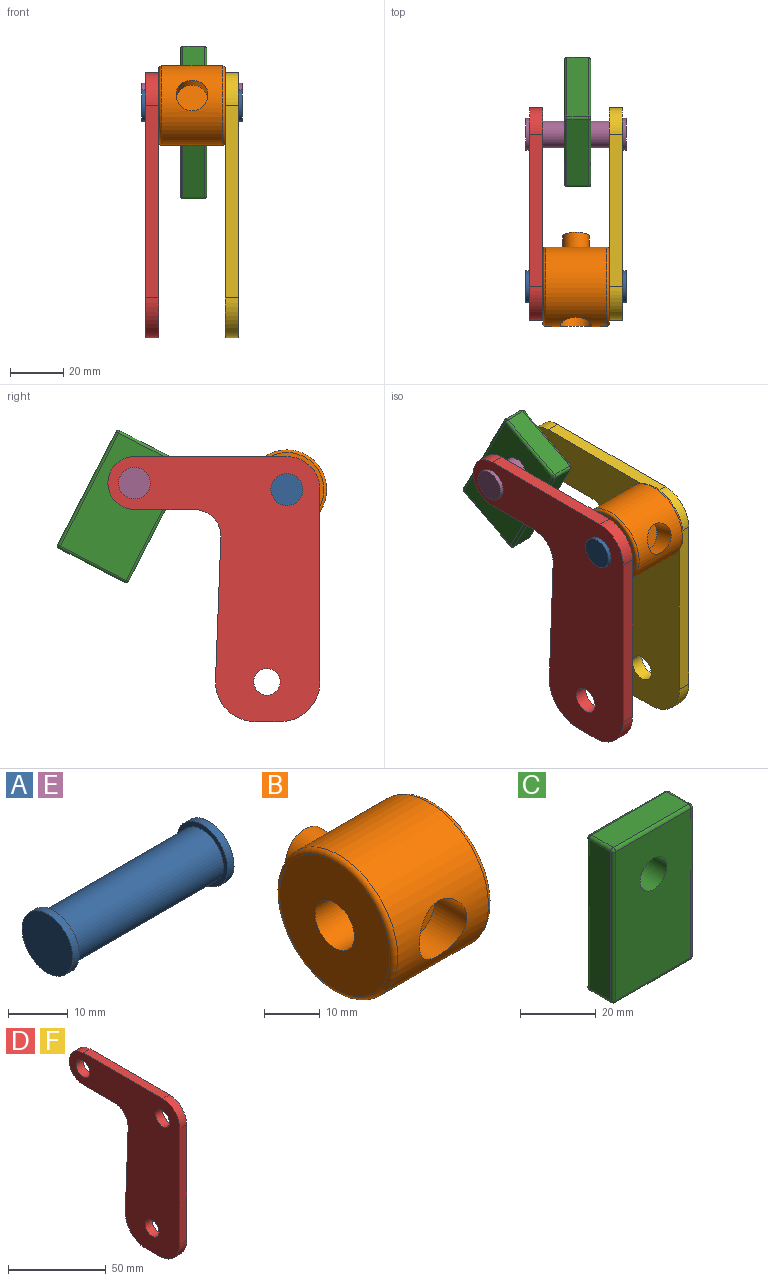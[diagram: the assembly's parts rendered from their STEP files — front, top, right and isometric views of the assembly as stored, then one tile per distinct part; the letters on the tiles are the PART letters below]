
ASSEMBLY  parts=6 mates=6
PART A: 7 faces, bbox 38x12x12 mm
  f0: plane 12x12mm, normal (1,0,0), area 113.1mm2, adj f1
  f1: cylinder r=6mm len=12mm, axis (-1,0,0), area 56.5mm2, adj f0,f2
  f2: plane 12x12mm, normal (-1,0,0), area 34.6mm2, adj f1,f3
  f3: cylinder r=5mm len=35mm, axis (-1,0,0), area 1099.6mm2, adj f2,f4
  f4: plane 12x12mm, normal (1,0,0), area 34.6mm2, adj f3,f5
  f5: cylinder r=6mm len=12mm, axis (-1,0,0), area 56.5mm2, adj f4,f6
  f6: plane 12x12mm, normal (-1,0,0), area 113.1mm2, adj f5
PART B: 10 faces, bbox 25x36.2x32.5 mm
  f0: cylinder r=5mm len=25mm, axis (-1,0,0), area 785.4mm2, adj f2,f3
  f1: cylinder r=15mm len=30mm, axis (-1,0,0), area 1972.8mm2, adj f4,f5,f6,f8
  f2: plane 28x28mm, normal (1,0,0), area 537.2mm2, adj f0,f5
  f3: plane 28x28mm, normal (-1,0,0), area 537.2mm2, adj f0,f4
  f4: torus R=14mm, axis (1,0,0), area 144.5mm2, adj f1,f3
  f5: torus R=14mm, axis (1,0,0), area 144.5mm2, adj f1,f2
  f6: cylinder r=6mm len=12mm, axis (0,-1,0), area 278.3mm2, adj f1,f7
  f7: plane 12x12mm, normal (0,-1,0), area 113.1mm2, adj f6
  f8: cylinder r=5mm len=10mm, axis (0,-1,0), area 170.5mm2, adj f1,f9
  f9: plane 10x10mm, normal (0,1,0), area 78.5mm2, adj f8
PART C: 27 faces, bbox 30x10x50 mm
  f0: plane 48x8mm, normal (-1,0,0), area 384mm2, adj f15,f20,f23,f26
  f1: plane 28x8mm, normal (0,0,-1), area 224mm2, adj f12,f21,f22,f26
  f2: plane 48x8mm, normal (1,0,0), area 384mm2, adj f7,f11,f12,f13
  f3: cylinder r=5mm len=10mm, axis (0,1,0), area 314.2mm2, adj f5,f6
  f4: plane 28x8mm, normal (0,0,1), area 224mm2, adj f7,f10,f14,f15
  f5: plane 48x28mm, normal (0,-1,0), area 1265.5mm2, adj f3,f10,f11,f20,f21
  f6: plane 48x28mm, normal (0,1,0), area 1265.5mm2, adj f3,f13,f14,f22,f23
  f7: cylinder r=1mm len=8mm, axis (0,1,0), area 12.6mm2, adj f2,f4,f8,f9
  f8: sphere r=1mm, area 1.6mm2, adj f7,f10,f11
  f9: sphere r=1mm, area 1.6mm2, adj f7,f13,f14
  f10: cylinder r=1mm len=28mm, axis (1,0,0), area 44mm2, adj f4,f5,f8,f16
  f11: cylinder r=1mm len=48mm, axis (0,0,-1), area 75.4mm2, adj f2,f5,f8,f17
  f12: cylinder r=1mm len=8mm, axis (0,1,0), area 12.6mm2, adj f1,f2,f17,f18
  f13: cylinder r=1mm len=48mm, axis (0,0,1), area 75.4mm2, adj f2,f6,f9,f18
  f14: cylinder r=1mm len=28mm, axis (-1,0,0), area 44mm2, adj f4,f6,f9,f19
  f15: cylinder r=1mm len=8mm, axis (0,1,0), area 12.6mm2, adj f0,f4,f16,f19
  f16: sphere r=1mm, area 1.6mm2, adj f10,f15,f20
  f17: sphere r=1mm, area 1.6mm2, adj f11,f12,f21
  f18: sphere r=1mm, area 1.6mm2, adj f12,f13,f22
  f19: sphere r=1mm, area 1.6mm2, adj f14,f15,f23
  f20: cylinder r=1mm len=48mm, axis (0,0,1), area 75.4mm2, adj f0,f5,f16,f24
  f21: cylinder r=1mm len=28mm, axis (-1,0,0), area 44mm2, adj f1,f5,f17,f24
  f22: cylinder r=1mm len=28mm, axis (1,0,0), area 44mm2, adj f1,f6,f18,f25
  f23: cylinder r=1mm len=48mm, axis (0,0,-1), area 75.4mm2, adj f0,f6,f19,f25
  f24: sphere r=1mm, area 1.6mm2, adj f20,f21,f26
  f25: sphere r=1mm, area 1.6mm2, adj f22,f23,f26
  f26: cylinder r=1mm len=8mm, axis (0,1,0), area 12.6mm2, adj f0,f1,f24,f25
PART D: 15 faces, bbox 5x80x100 mm
  f0: plane 72.5x5mm, normal (0,-1,0), area 362.5mm2, adj f8,f9,f12,f14
  f1: plane 9.43x5mm, normal (0,0,-1), area 47.1mm2, adj f8,f9,f12,f13
  f2: plane 54.06x5mm, normal (0,1,0.04), area 270.5mm2, adj f8,f9,f10,f13
  f3: plane 22.62x5mm, normal (0,0,-1), area 113.1mm2, adj f8,f9,f10,f11
  f4: cylinder r=5mm len=10mm, axis (-1,0,0), area 157.1mm2, adj f8,f9
  f5: cylinder r=5mm len=10mm, axis (-1,0,0), area 157.1mm2, adj f8,f9
  f6: plane 57.5x5mm, normal (0,0,1), area 287.5mm2, adj f8,f9,f11,f14
  f7: cylinder r=5mm len=10mm, axis (-1,0,0), area 157.1mm2, adj f8,f9
  f8: plane 100x80mm, normal (1,0,0), area 4290.4mm2, adj f0,f1,f2,f3,f4,f5,f6,f7
  f9: plane 100x80mm, normal (-1,0,0), area 4290.4mm2, adj f0,f1,f2,f3,f4,f5,f6,f7
  f10: cylinder r=10mm len=10.37mm, axis (1,0,0), area 80.4mm2, adj f2,f3,f8,f9
  f11: cylinder r=10mm len=20mm, axis (-1,0,0), area 157.1mm2, adj f3,f6,f8,f9
  f12: cylinder r=15mm len=15mm, axis (-1,0,0), area 117.8mm2, adj f0,f1,f8,f9
  f13: cylinder r=15mm len=15.56mm, axis (-1,0,0), area 120.6mm2, adj f1,f2,f8,f9
  f14: cylinder r=12.5mm len=12.5mm, axis (-1,0,0), area 98.2mm2, adj f0,f6,f8,f9
PART E: same geometry as A
PART F: same geometry as D
PLACE A t=(-12.5,12.5,-12.5)mm
PLACE B rot(axis=(-1,0,0),16.3deg) t=(-12.5,12.5,-12.5)mm
PLACE C rot(axis=(0.23,-0.23,0.95),93.2deg) t=(-11.91,72.76,-47.98)mm
PLACE D t=(-30,0,0)mm
PLACE E rot(axis=(1,0,0),27.3deg) t=(-12.5,70,-10)mm
PLACE F at identity fixed
MATE cylindrical A.f1 <-> F.f4  axis (-1,0,0) through (5,12.5,-12.5)mm
MATE cylindrical E.f1 <-> D.f5  axis (-1,0,0) through (-30,70,-10)mm
MATE cylindrical E.f1 <-> F.f5  axis (-1,0,0) through (5,70,-10)mm
MATE cylindrical B.f0 <-> D.f4  axis (-1,0,0) through (-25,12.5,-12.5)mm
MATE slider C.f3 <-> E.f1  axis (-1,0,0) through (-11.91,70,-10)mm
MATE cylindrical D.f4 <-> A.f1  axis (-1,0,0) through (-30,12.5,-12.5)mm
